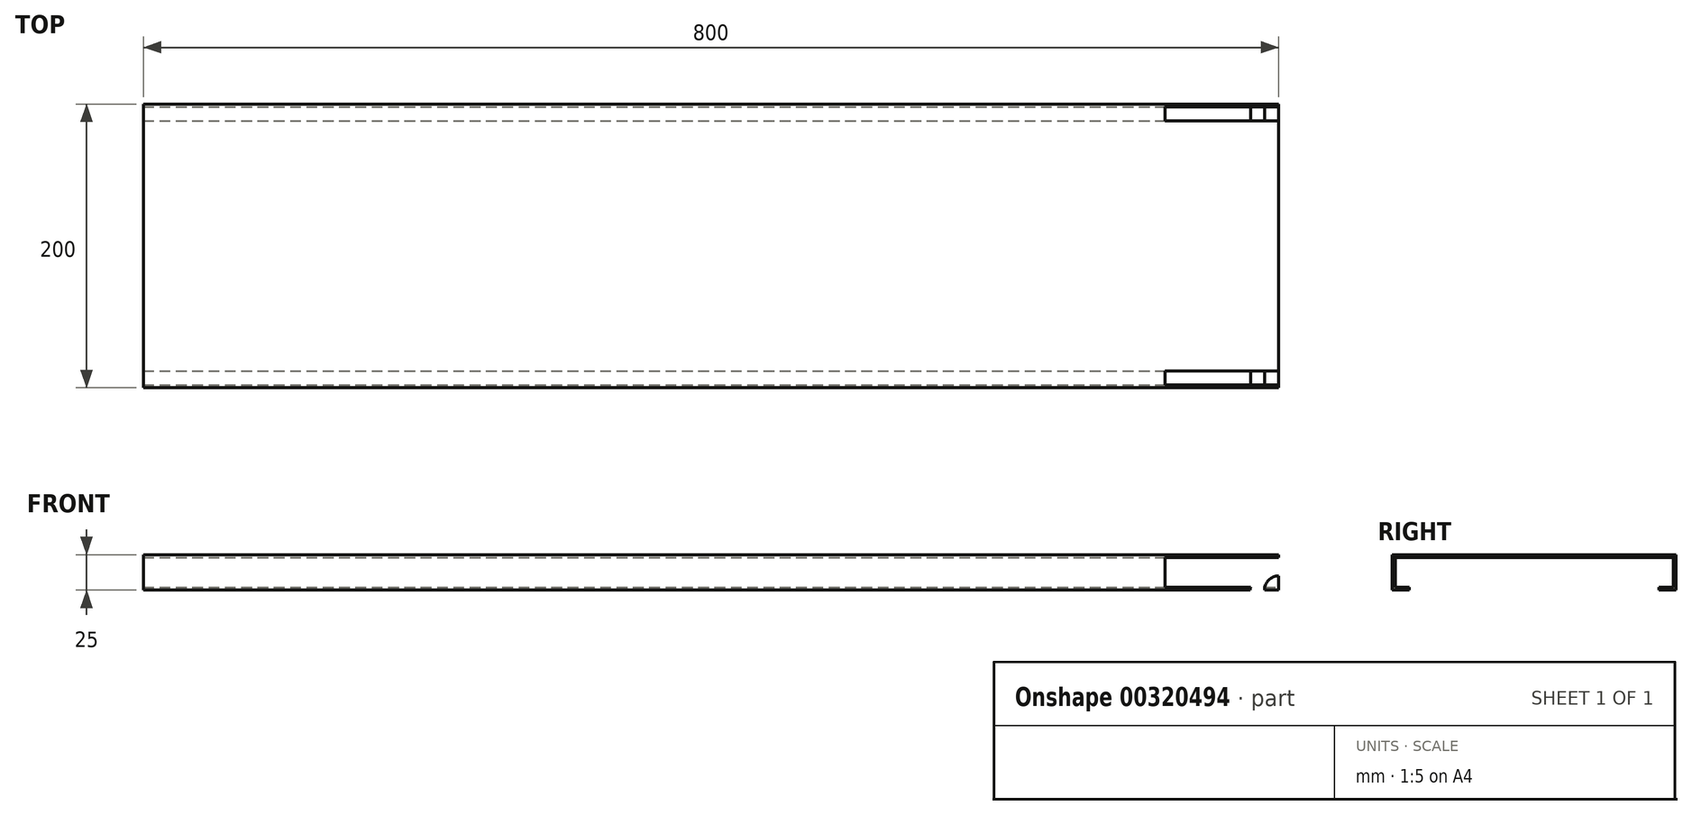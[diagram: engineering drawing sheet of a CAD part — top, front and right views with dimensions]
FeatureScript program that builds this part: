
annotation { "Feature Type Name" : "Feature", "Feature Type Description" : "" }
export const myFeature = defineFeature(function(context is Context, id is Id, definition is map)
    precondition{}
    {
        {
            var Q0;
            Q0=qCreatedBy(makeId("Right.planeOp"),FACE);
            var sketch = newSketch(context, id + "F0", { "sketchPlane" : qUnion([Q0])});
            skLineSegment(sketch, "E0", {"start": v(-91.3, -39.22) * mm, "end": v(-103.3, -39.22) * mm});
            skLineSegment(sketch, "E1", {"start": v(-103.3, -39.22) * mm, "end": v(-103.3, -14.22) * mm});
            skLineSegment(sketch, "E2", {"start": v(-103.3, -14.22) * mm, "end": v(96.7, -14.22) * mm});
            skLineSegment(sketch, "E3", {"start": v(96.7, -14.22) * mm, "end": v(96.7, -39.22) * mm});
            skLineSegment(sketch, "E4", {"start": v(96.7, -39.22) * mm, "end": v(84.7, -39.22) * mm});
            skLineSegment(sketch, "E5", {"start": v(84.7, -39.22) * mm, "end": v(84.7, -37.22) * mm});
            skLineSegment(sketch, "E6", {"start": v(84.7, -37.22) * mm, "end": v(94.7, -37.22) * mm});
            skLineSegment(sketch, "E7", {"start": v(94.7, -37.22) * mm, "end": v(94.7, -16.22) * mm});
            skLineSegment(sketch, "E8", {"start": v(94.7, -16.22) * mm, "end": v(-101.3, -16.22) * mm});
            skLineSegment(sketch, "E9", {"start": v(-101.3, -16.22) * mm, "end": v(-101.3, -37.22) * mm});
            skLineSegment(sketch, "E10", {"start": v(-101.3, -37.22) * mm, "end": v(-91.3, -37.22) * mm});
            skLineSegment(sketch, "E11", {"start": v(-91.3, -37.22) * mm, "end": v(-91.3, -39.22) * mm});
            skSolve(sketch);
        }
        {
            var Q0;
            Q0=makeQuery(id+"F0.imprint","IMPRINT",FACE,{"disambiguationData":[TD([[makeQuery(id+"F0.imprint","IMPRINT",EDGE,{"derivedFrom":sQuery(id+"F0.wireOp",EDGE,"E0")}),-1.0]])]});
            extrude(context, id + "F1", {"entities" : qUnion([Q0]), "oppositeDirection" : true, "depth" : 800 * mm});
        }
        {
            var Q0;
            Q0=makeQuery(id+"F1.opExtrude","SWEPT_FACE",FACE,{"disambiguationData":[OSD([sQuery(id+"F0.wireOp",EDGE,"E7")])]});
            var sketch = newSketch(context, id + "F2", { "sketchPlane" : qUnion([Q0])});
            skLineSegment(sketch, "E12", {"start": v(0, -37.22) * mm, "end": v(0, -39.22) * mm});
            skLineSegment(sketch, "E13", {"start": v(-20, -39.22) * mm, "end": v(-80, -39.22) * mm});
            skLineSegment(sketch, "E14", {"start": v(-80, -39.22) * mm, "end": v(-80, -26.22) * mm});
            skLineSegment(sketch, "E15", {"start": v(-80, -26.22) * mm, "end": v(-50, -26.22) * mm});
            skLineSegment(sketch, "E16", {"start": v(-50, -26.22) * mm, "end": v(-20, -39.22) * mm});
            skSolve(sketch);
        }
        {
            var Q0;
            {var subQ0=sQuery(id+"F2.wireOp",EDGE,"E15");Q0=makeQuery(id+"F2.imprint","IMPRINT",FACE,{"disambiguationData":[TD([[makeQuery(id+"F2.imprint","IMPRINT",EDGE,{"derivedFrom":subQ0}),-1.0]])]});}
            extrude(context, id + "F3", {"entities" : qUnion([Q0]), "depth" : 10 * mm});
        }
        {
            var Q0;
            Q0=makeQuery(id+"F3GGlgdsp50E81Y_1.boolean.opBoolean","MERGE",FACE,{"derivedFrom":[makeQuery(id+"F1.opExtrude","SWEPT_FACE",FACE,{"disambiguationData":[OSD([sQuery(id+"F0.wireOp",EDGE,"E5")])]}),makeQuery(id+"F3GGlgdsp50E81Y_1.opExtrude","CAP_FACE",FACE,{"disambiguationData":[OSD([sQuery(id+"F2.wireOp",EDGE,"dfxmLzlp-oZsF-CoDL-Eu9e-fH9JU5qJ0lIo"),sQuery(id+"F2.wireOp",EDGE,"FmUmcMun-TIzK-RcXF-JOKL-ZLxRyT1Zl2QG"),sQuery(id+"F2.wireOp",EDGE,"hh3lwnsW-zyfY-lDS1-MBsT-0XLG6f722Eiz"),sQuery(id+"F2.wireOp",EDGE,"9YCPTIap-H3Gf-WF8u-q0Cc-Rv3sE4uuu8WY")])],"isStart":false})]});
            var sketch = newSketch(context, id + "F4", { "sketchPlane" : qUnion([Q0])});
            skLineSegment(sketch, "E17", {"start": v(-80, -37.22) * mm, "end": v(-19.9, -37.22) * mm});
            skArc(sketch, "E18", {"start": v(-19.9, -37.22) * mm, "mid": v(13.42, -54.06) * mm, "end": v(0, -19.22) * mm});
            skCircle(sketch, "E19", {"center": v(0, -39.22) * mm, "radius": 10 * mm});
            skLineSegment(sketch, "E20", {"start": v(0, -16.22) * mm, "end": v(0, -19.22) * mm});
            skLineSegment(sketch, "E21", {"start": v(0, -16.22) * mm, "end": v(-80, -16.22) * mm});
            skLineSegment(sketch, "E22", {"start": v(-80, -37.22) * mm, "end": v(-80, -16.22) * mm});
            skSolve(sketch);
        }
        {
            var Q0;
            {var subQ0=sQuery(id+"F4.wireOp",EDGE,"E18");var subQ4=sQuery(id+"F0.wireOp",EDGE,"E5");var subQ5=sQuery(id+"F0.wireOp",EDGE,"E4");var subQ8=makeQuery(id+"F1.opExtrude","SWEPT_EDGE",EDGE,{"disambiguationData":[OSD([subQ5,subQ4])]});var subQ9=makeQuery(id+"F4.imprint","INTERSECT",VERTEX,{"derivedFrom":[subQ8,subQ0]});Q0=makeQuery(id+"F4.imprint","IMPRINT",FACE,{"disambiguationData":[TD([[makeQuery(id+"F4.imprint","IMPRINT",EDGE,{"disambiguationData":[TD([[subQ9,-1.0]])],"derivedFrom":subQ8}),1.0]])]});}
            var Q1;
            {var subQ11=sQuery(id+"F4.wireOp",EDGE,"E20");Q1=makeQuery(id+"F4.imprint","IMPRINT",FACE,{"disambiguationData":[TD([[makeQuery(id+"F4.imprint","IMPRINT",EDGE,{"derivedFrom":subQ11}),-1.0]])]});}
            var Q2;
            {var subQ7=sQuery(id+"F2.wireOp",EDGE,"E15");var subQ10=makeQuery(id+"F3.opExtrude","CAP_EDGE",EDGE,{"disambiguationData":[OSD([subQ7])],"isStart":false});Q2=makeQuery(id+"F4.imprint","IMPRINT",FACE,{"disambiguationData":[TD([[makeQuery(id+"F4.imprint","IMPRINT",EDGE,{"derivedFrom":subQ10}),-1.0]])]});}
            extrude(context, id + "F5", {"entities" : qUnion([Q0, Q1, Q2]), "depth" : 10 * mm});
        }
        {
            var Q0;
            Q0=makeQuery(id+"F1.opExtrude","SWEPT_FACE",FACE,{"disambiguationData":[OSD([sQuery(id+"F0.wireOp",EDGE,"E2")])]});
            var sketch = newSketch(context, id + "F6", { "sketchPlane" : qUnion([Q0])});
            skLineSegment(sketch, "E23", {"start": v(0, 96.7) * mm, "end": v(0, 94.7) * mm});
            skLineSegment(sketch, "E24", {"start": v(0, 94.7) * mm, "end": v(-80, 94.7) * mm});
            skLineSegment(sketch, "E25", {"start": v(-80, 94.7) * mm, "end": v(-80, 96.7) * mm});
            skLineSegment(sketch, "E26", {"start": v(-80, 94.7) * mm, "end": v(-80, 84.7) * mm});
            skLineSegment(sketch, "E27", {"start": v(-80, 84.7) * mm, "end": v(0, 84.7) * mm});
            skLineSegment(sketch, "E28", {"start": v(0, 84.7) * mm, "end": v(0, 94.7) * mm});
            skLineSegment(sketch, "E29", {"start": v(0, -103.3) * mm, "end": v(0, -101.3) * mm});
            skLineSegment(sketch, "E30", {"start": v(0, -101.3) * mm, "end": v(0, -91.3) * mm});
            skLineSegment(sketch, "E31", {"start": v(0, -91.3) * mm, "end": v(-80, -91.3) * mm});
            skLineSegment(sketch, "E32", {"start": v(0, -101.3) * mm, "end": v(-80, -101.3) * mm});
            skLineSegment(sketch, "E33", {"start": v(-80, -91.3) * mm, "end": v(-80, -101.3) * mm});
            skSolve(sketch);
        }
        {
            var Q0;
            Q0=makeQuery(id+"F6.imprint","IMPRINT",FACE,{"disambiguationData":[TD([[makeQuery(id+"F6.imprint","IMPRINT",EDGE,{"derivedFrom":sQuery(id+"F6.wireOp",EDGE,"E24")}),1.0]])]});
            extrude(context, id + "F7", {"entities" : qUnion([Q0]), "operationType" : NewBodyOperationType.REMOVE, "oppositeDirection" : true, "depth" : 2 * mm});
        }
        {
            var Q0;
            Q0=makeQuery(id+"F1.opExtrude","SWEPT_FACE",FACE,{"disambiguationData":[OSD([sQuery(id+"F0.wireOp",EDGE,"E9")])]});
            var sketch = newSketch(context, id + "F8", { "sketchPlane" : qUnion([Q0])});
            skLineSegment(sketch, "E34", {"start": v(80, -39.22) * mm, "end": v(80, -26.22) * mm});
            skLineSegment(sketch, "E35.MirrorCS", {"start": v(0, -37.22) * mm, "end": v(0, -39.22) * mm});
            skLineSegment(sketch, "E36.MirrorCS", {"start": v(50, -26.22) * mm, "end": v(20, -39.22) * mm});
            skLineSegment(sketch, "E37.MirrorCS", {"start": v(80, -26.22) * mm, "end": v(50, -26.22) * mm});
            skLineSegment(sketch, "E38.MirrorCS", {"start": v(20, -39.22) * mm, "end": v(80, -39.22) * mm});
            skSolve(sketch);
        }
        {
            var Q0;
            {var subQ0=sQuery(id+"F8.wireOp",EDGE,"E37.MirrorCS");Q0=makeQuery(id+"F8.imprint","IMPRINT",FACE,{"disambiguationData":[TD([[makeQuery(id+"F8.imprint","IMPRINT",EDGE,{"derivedFrom":subQ0}),1.0]])]});}
            extrude(context, id + "F9", {"entities" : qUnion([Q0]), "depth" : 10 * mm});
        }
        {
            var Q0;
            Q0=makeQuery(id+"F9.boolean.opBoolean","MERGE",FACE,{"derivedFrom":[makeQuery(id+"F1.opExtrude","SWEPT_FACE",FACE,{"disambiguationData":[OSD([sQuery(id+"F0.wireOp",EDGE,"E11")])]}),makeQuery(id+"F9.opExtrude","CAP_FACE",FACE,{"disambiguationData":[OSD([sQuery(id+"F0.wireOp",EDGE,"E9"),sQuery(id+"F0.wireOp",EDGE,"E10"),sQuery(id+"F8.wireOp",EDGE,"E34"),sQuery(id+"F8.wireOp",EDGE,"E37.MirrorCS"),sQuery(id+"F8.wireOp",EDGE,"E36.MirrorCS")])],"isStart":false})]});
            var sketch = newSketch(context, id + "F10", { "sketchPlane" : qUnion([Q0])});
            skLineSegment(sketch, "E39", {"start": v(80, -37.22) * mm, "end": v(80, -16.22) * mm});
            skLineSegment(sketch, "E40.MirrorCS", {"start": v(0, -16.22) * mm, "end": v(0, -19.22) * mm});
            skLineSegment(sketch, "E41.MirrorCS", {"start": v(80, -37.22) * mm, "end": v(19.9, -37.22) * mm});
            skArc(sketch, "E42.MirrorCS", {"start": v(19.9, -37.22) * mm, "mid": v(-13.42, -54.06) * mm, "end": v(0, -19.22) * mm});
            skCircle(sketch, "E43.MirrorC", {"center": v(0, -39.22) * mm, "radius": 10 * mm});
            skLineSegment(sketch, "E44.MirrorCS", {"start": v(0, -16.22) * mm, "end": v(80, -16.22) * mm});
            skSolve(sketch);
        }
        {
            var Q0;
            {var subQ1=sQuery(id+"F0.wireOp",EDGE,"E11");var subQ2=sQuery(id+"F0.wireOp",EDGE,"E0");var subQ3=makeQuery(id+"F1.opExtrude","SWEPT_EDGE",EDGE,{"disambiguationData":[OSD([subQ2,subQ1])]});var subQ10=sQuery(id+"F10.wireOp",EDGE,"E42.MirrorCS");var subQ12=makeQuery(id+"F10.imprint","INTERSECT",VERTEX,{"derivedFrom":[subQ3,subQ10]});Q0=makeQuery(id+"F10.imprint","IMPRINT",FACE,{"disambiguationData":[TD([[makeQuery(id+"F10.imprint","IMPRINT",EDGE,{"disambiguationData":[TD([[subQ12,-1.0]])],"derivedFrom":subQ3}),-1.0]])]});}
            var Q1;
            {var subQ12=sQuery(id+"F10.wireOp",EDGE,"E40.MirrorCS");Q1=makeQuery(id+"F10.imprint","IMPRINT",FACE,{"disambiguationData":[TD([[makeQuery(id+"F10.imprint","IMPRINT",EDGE,{"derivedFrom":subQ12}),1.0]])]});}
            var Q2;
            {var subQ1=makeQuery(id+"F9.opExtrude","CAP_EDGE",EDGE,{"disambiguationData":[OSD([sQuery(id+"F8.wireOp",EDGE,"E37.MirrorCS")])],"isStart":false});Q2=makeQuery(id+"F10.imprint","IMPRINT",FACE,{"disambiguationData":[TD([[makeQuery(id+"F10.imprint","IMPRINT",EDGE,{"derivedFrom":subQ1}),1.0]])]});}
            extrude(context, id + "F11", {"entities" : qUnion([Q0, Q1, Q2]), "depth" : 10 * mm});
        }
        {
            var Q0;
            Q0=makeQuery(id+"F11.opExtrude","CAP_FACE",FACE,{"disambiguationData":[OSD([sQuery(id+"F10.wireOp",EDGE,"E39"),sQuery(id+"F10.wireOp",EDGE,"E40.MirrorCS"),sQuery(id+"F10.wireOp",EDGE,"E44.MirrorCS"),sQuery(id+"F10.wireOp",EDGE,"E43.MirrorC"),sQuery(id+"F10.wireOp",EDGE,"E42.MirrorCS"),sQuery(id+"F10.wireOp",EDGE,"E41.MirrorCS")])],"isStart":false});
            var sketch = newSketch(context, id + "F12", { "sketchPlane" : qUnion([Q0])});
            skCircle(sketch, "E45", {"center": v(0, -39.22) * mm, "radius": 10 * mm});
            skSolve(sketch);
        }
        {
            var Q0;
            Q0=makeQuery(id+"F12.imprint","IMPRINT",FACE,{"disambiguationData":[TD([[makeQuery(id+"F12.imprint","IMPRINT",EDGE,{"derivedFrom":sQuery(id+"F12.wireOp",EDGE,"E45")}),-1.0]])]});
            extrude(context, id + "F13", {"entities" : qUnion([Q0]), "operationType" : NewBodyOperationType.REMOVE, "oppositeDirection" : true, "depth" : 50 * mm, "hasSecondDirection" : true, "secondDirectionOppositeDirection" : false, "secondDirectionDepth" : 250 * mm});
        }
        {
            var Q0;
            Q0=makeQuery(id+"F6.imprint","IMPRINT",FACE,{"disambiguationData":[TD([[makeQuery(id+"F6.imprint","IMPRINT",EDGE,{"derivedFrom":sQuery(id+"F6.wireOp",EDGE,"E30")}),1.0]])]});
            extrude(context, id + "F14", {"entities" : qUnion([Q0]), "operationType" : NewBodyOperationType.REMOVE, "oppositeDirection" : true, "depth" : 2 * mm});
        }
    });
